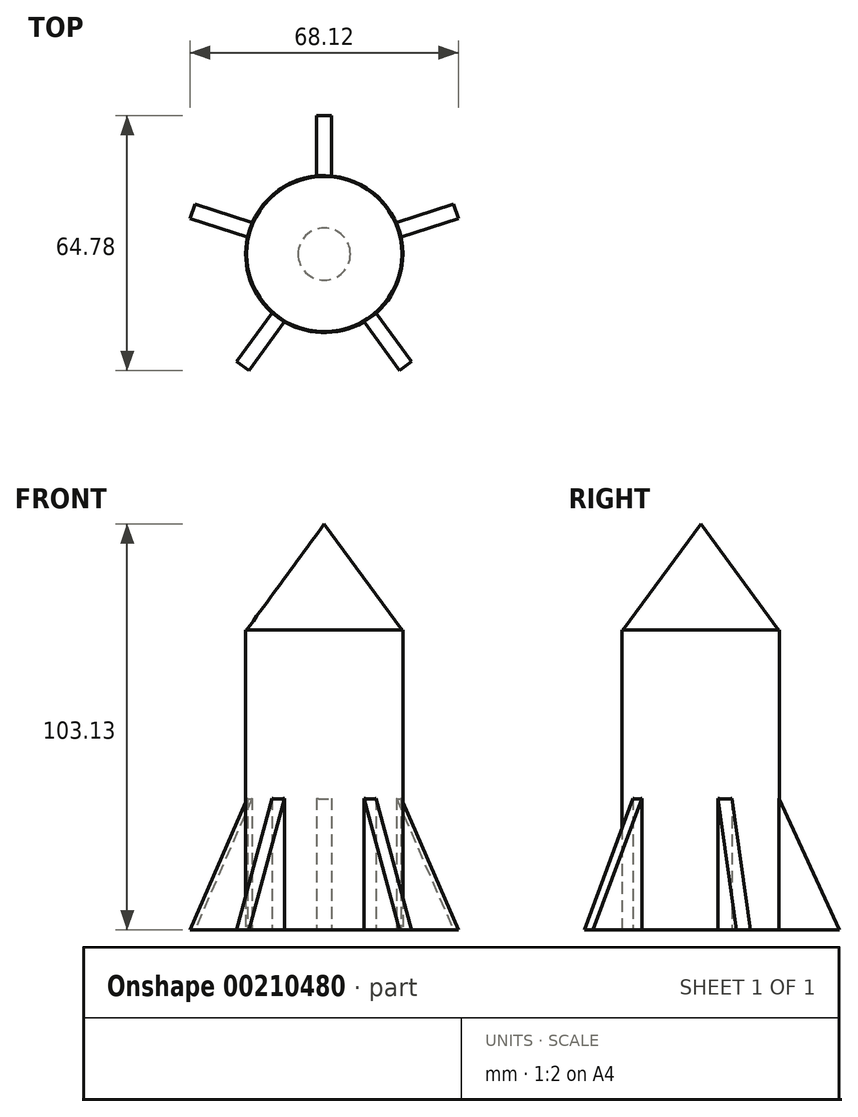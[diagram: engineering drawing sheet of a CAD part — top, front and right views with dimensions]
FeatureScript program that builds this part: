
annotation { "Feature Type Name" : "Feature", "Feature Type Description" : "" }
export const myFeature = defineFeature(function(context is Context, id is Id, definition is map)
    precondition{}
    {
        {
            var Q0;
            Q0=qCreatedBy(makeId("Top.planeOp"),FACE);
            var sketch = newSketch(context, id + "F0", { "sketchPlane" : qUnion([Q0])});
            skCircle(sketch, "E0", {"center": v(0, 0) * mm, "radius": 19.96 * mm});
            skSolve(sketch);
        }
        {
            var Q0;
            Q0 = qSketchRegion(id + "F0", true);
            extrude(context, id + "F1", {"entities" : qUnion([Q0]), "depth" : 76.2 * mm});
        }
        {
            var Q0;
            Q0=qCreatedBy(makeId("Right.planeOp"),FACE);
            var sketch = newSketch(context, id + "F2", { "sketchPlane" : qUnion([Q0])});
            skLineSegment(sketch, "E1", {"start": v(11.91, 0) * mm, "end": v(11.91, 50.8) * mm});
            skLineSegment(sketch, "E2", {"start": v(11.91, 50.8) * mm, "end": v(35.2, 0) * mm});
            skLineSegment(sketch, "E3", {"start": v(35.2, 0) * mm, "end": v(11.91, 0) * mm});
            skSolve(sketch);
        }
        {
            var Q0;
            Q0 = qSketchRegion(id + "F2", true);
            extrude(context, id + "F3", {"entities" : qUnion([Q0]), "operationType" : NewBodyOperationType.ADD, "endBound" : BoundingType.SYMMETRIC, "oppositeDirection" : true, "depth" : 3.8 * mm});
        }
        {
            var Q0;
            Q0=makeQuery(id+"F1.opExtrude","SWEPT_BODY",BODY,{"disambiguationData":[OSD([sQuery(id+"F0.wireOp",EDGE,"E0")])]});
            var Q1;
            Q1=makeQuery(id+"F1.opExtrude","SWEPT_FACE",FACE,{"disambiguationData":[OSD([sQuery(id+"F0.wireOp",EDGE,"E0")])]});
            circularPattern(context, id + "F4", {"entities" : qUnion([Q0]), "axis" : qUnion([Q1]), "angle" : 360 * degree, "instanceCount" : 5, "equalSpace" : true});
        }
        {
            var Q0;
            Q0=qCreatedBy(makeId("Right.planeOp"),FACE);
            var sketch = newSketch(context, id + "F5", { "sketchPlane" : qUnion([Q0])});
            skLineSegment(sketch, "E4", {"start": v(0, 76.3) * mm, "end": v(0, 103.13) * mm});
            skLineSegment(sketch, "E5", {"start": v(0, 103.13) * mm, "end": v(-19.87, 76) * mm});
            skLineSegment(sketch, "E6", {"start": v(-19.87, 76) * mm, "end": v(0, 76.3) * mm});
            skSolve(sketch);
        }
        {
            var Q0;
            Q0 = qSketchRegion(id + "F5", true);
            var Q1;
            Q1=sQuery(id+"F5.wireOp",EDGE,"E4");
            revolve(context, id + "F6", {"operationType" : NewBodyOperationType.ADD, "entities" : qUnion([Q0]), "axis" : qUnion([Q1]), "revolveType" : RevolveType.FULL});
        }
    });
